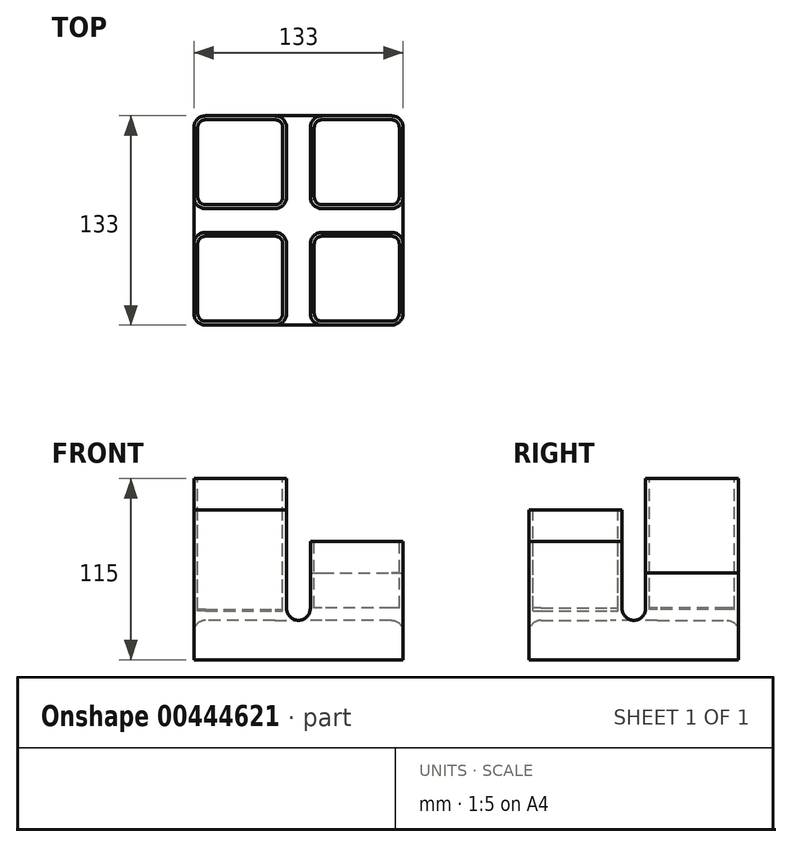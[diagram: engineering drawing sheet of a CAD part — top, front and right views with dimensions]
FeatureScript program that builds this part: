
annotation { "Feature Type Name" : "Feature", "Feature Type Description" : "" }
export const myFeature = defineFeature(function(context is Context, id is Id, definition is map)
    precondition{}
    {
        {
            var Q0;
            Q0=qCreatedBy(makeId("Top.planeOp"),FACE);
            var sketch = newSketch(context, id + "F0", { "sketchPlane" : qUnion([Q0])});
            skLineSegment(sketch, "E0", {"start": v(-102.34, 64.05) * mm, "end": v(-102.34, -68.95) * mm});
            skLineSegment(sketch, "E1", {"start": v(-102.34, -68.95) * mm, "end": v(30.66, -68.95) * mm});
            skLineSegment(sketch, "E2", {"start": v(30.66, -68.95) * mm, "end": v(30.66, 64.05) * mm});
            skLineSegment(sketch, "E3", {"start": v(-102.34, 64.05) * mm, "end": v(30.66, 64.05) * mm});
            skSolve(sketch);
        }
        {
            var Q0;
            Q0 = qSketchRegion(id + "F0", true);
            extrude(context, id + "F1", {"entities" : qUnion([Q0]), "depth" : 25 * mm});
        }
        {
            var Q0;
            Q0=makeQuery(id+"F1.opExtrude","CAP_FACE",FACE,{"disambiguationData":[OSD([sQuery(id+"F0.wireOp",EDGE,"E0"),sQuery(id+"F0.wireOp",EDGE,"E1"),sQuery(id+"F0.wireOp",EDGE,"E2"),sQuery(id+"F0.wireOp",EDGE,"E3")])],"isStart":false});
            var sketch = newSketch(context, id + "F2", { "sketchPlane" : qUnion([Q0])});
            skLineSegment(sketch, "E4", {"start": v(-102.34, 64.05) * mm, "end": v(-102.34, 5.05) * mm});
            skLineSegment(sketch, "E5", {"start": v(-102.34, 5.05) * mm, "end": v(-43.34, 5.05) * mm});
            skLineSegment(sketch, "E6", {"start": v(-43.34, 5.05) * mm, "end": v(-43.34, 64.05) * mm});
            skLineSegment(sketch, "E7", {"start": v(-43.34, 64.05) * mm, "end": v(-102.34, 64.05) * mm});
            skSolve(sketch);
        }
        {
            var Q0;
            Q0=makeQuery(id+"F2.imprint","IMPRINT",FACE,{"disambiguationData":[TD([[makeQuery(id+"F2.imprint","IMPRINT",EDGE,{"derivedFrom":sQuery(id+"F2.wireOp",EDGE,"E4")}),1.0]])]});
            extrude(context, id + "F3", {"entities" : qUnion([Q0]), "operationType" : NewBodyOperationType.ADD, "depth" : 90 * mm});
        }
        {
            var Q0;
            Q0=makeQuery(id+"F1.opExtrude","CAP_FACE",FACE,{"disambiguationData":[OSD([sQuery(id+"F0.wireOp",EDGE,"E0"),sQuery(id+"F0.wireOp",EDGE,"E1"),sQuery(id+"F0.wireOp",EDGE,"E2"),sQuery(id+"F0.wireOp",EDGE,"E3")])],"isStart":false});
            var sketch = newSketch(context, id + "F4", { "sketchPlane" : qUnion([Q0])});
            skLineSegment(sketch, "E8", {"start": v(-102.34, -9.95) * mm, "end": v(-43.34, -9.95) * mm});
            skLineSegment(sketch, "E9", {"start": v(-43.34, -9.95) * mm, "end": v(-43.34, -68.95) * mm});
            skLineSegment(sketch, "E10", {"start": v(-43.34, -68.95) * mm, "end": v(-102.34, -68.95) * mm});
            skLineSegment(sketch, "E11", {"start": v(-102.34, -68.95) * mm, "end": v(-102.34, -9.95) * mm});
            skSolve(sketch);
        }
        {
            var Q0;
            Q0=makeQuery(id+"F4.imprint","IMPRINT",FACE,{"disambiguationData":[TD([[makeQuery(id+"F4.imprint","IMPRINT",EDGE,{"derivedFrom":sQuery(id+"F4.wireOp",EDGE,"E8")}),-1.0]])]});
            extrude(context, id + "F5", {"entities" : qUnion([Q0]), "operationType" : NewBodyOperationType.ADD, "depth" : 70 * mm});
        }
        {
            var Q0;
            Q0=makeQuery(id+"F1.opExtrude","CAP_FACE",FACE,{"disambiguationData":[OSD([sQuery(id+"F0.wireOp",EDGE,"E0"),sQuery(id+"F0.wireOp",EDGE,"E1"),sQuery(id+"F0.wireOp",EDGE,"E2"),sQuery(id+"F0.wireOp",EDGE,"E3")])],"isStart":false});
            var sketch = newSketch(context, id + "F6", { "sketchPlane" : qUnion([Q0])});
            skLineSegment(sketch, "E12", {"start": v(-28.34, -68.95) * mm, "end": v(-28.34, -9.95) * mm});
            skLineSegment(sketch, "E13", {"start": v(-28.34, -9.95) * mm, "end": v(30.66, -9.95) * mm});
            skLineSegment(sketch, "E14", {"start": v(30.66, -9.95) * mm, "end": v(30.66, -68.95) * mm});
            skLineSegment(sketch, "E15", {"start": v(30.66, -68.95) * mm, "end": v(-28.34, -68.95) * mm});
            skSolve(sketch);
        }
        {
            var Q0;
            Q0=makeQuery(id+"F6.imprint","IMPRINT",FACE,{"disambiguationData":[TD([[makeQuery(id+"F6.imprint","IMPRINT",EDGE,{"derivedFrom":sQuery(id+"F6.wireOp",EDGE,"E12")}),-1.0]])]});
            extrude(context, id + "F7", {"entities" : qUnion([Q0]), "operationType" : NewBodyOperationType.ADD, "depth" : 50 * mm});
        }
        {
            var Q0;
            Q0=makeQuery(id+"F1.opExtrude","CAP_FACE",FACE,{"disambiguationData":[OSD([sQuery(id+"F0.wireOp",EDGE,"E0"),sQuery(id+"F0.wireOp",EDGE,"E1"),sQuery(id+"F0.wireOp",EDGE,"E2"),sQuery(id+"F0.wireOp",EDGE,"E3")])],"isStart":false});
            var sketch = newSketch(context, id + "F8", { "sketchPlane" : qUnion([Q0])});
            skLineSegment(sketch, "E16", {"start": v(-28.34, 64.05) * mm, "end": v(-28.34, 5.05) * mm});
            skLineSegment(sketch, "E17", {"start": v(-28.34, 5.05) * mm, "end": v(30.66, 5.05) * mm});
            skLineSegment(sketch, "E18", {"start": v(30.66, 5.05) * mm, "end": v(30.66, 64.05) * mm});
            skLineSegment(sketch, "E19", {"start": v(30.66, 64.05) * mm, "end": v(-28.34, 64.05) * mm});
            skSolve(sketch);
        }
        {
            var Q0;
            Q0=makeQuery(id+"F8.imprint","IMPRINT",FACE,{"disambiguationData":[TD([[makeQuery(id+"F8.imprint","IMPRINT",EDGE,{"derivedFrom":sQuery(id+"F8.wireOp",EDGE,"E16")}),1.0]])]});
            extrude(context, id + "F9", {"entities" : qUnion([Q0]), "operationType" : NewBodyOperationType.ADD, "depth" : 30 * mm});
        }
        {
            var Q0;
            Q0=makeQuery(id+"F9.opExtrude","SWEPT_EDGE",EDGE,{"disambiguationData":[OSD([sQuery(id+"F0.wireOp",EDGE,"E2"),sQuery(id+"F8.wireOp",EDGE,"E17"),sQuery(id+"F8.wireOp",EDGE,"E18")])]});
            var Q1;
            Q1=makeQuery(id+"F9.boolean.opBoolean","MERGE",EDGE,{"derivedFrom":[makeQuery(id+"F1.opExtrude","SWEPT_EDGE",EDGE,{"disambiguationData":[OSD([sQuery(id+"F0.wireOp",EDGE,"E2"),sQuery(id+"F0.wireOp",EDGE,"E3")])]}),makeQuery(id+"F9.opExtrude","SWEPT_EDGE",EDGE,{"disambiguationData":[OSD([sQuery(id+"F8.wireOp",EDGE,"E18"),sQuery(id+"F8.wireOp",EDGE,"E19")])]})]});
            var Q2;
            Q2=makeQuery(id+"F9.opExtrude","SWEPT_EDGE",EDGE,{"disambiguationData":[OSD([sQuery(id+"F0.wireOp",EDGE,"E3"),sQuery(id+"F8.wireOp",EDGE,"E16"),sQuery(id+"F8.wireOp",EDGE,"E19")])]});
            var Q3;
            Q3=makeQuery(id+"F9.opExtrude","SWEPT_EDGE",EDGE,{"disambiguationData":[OSD([sQuery(id+"F8.wireOp",EDGE,"E16"),sQuery(id+"F8.wireOp",EDGE,"E17")])]});
            var Q4;
            Q4=makeQuery(id+"F7.opExtrude","SWEPT_EDGE",EDGE,{"disambiguationData":[OSD([sQuery(id+"F0.wireOp",EDGE,"E2"),sQuery(id+"F6.wireOp",EDGE,"E13"),sQuery(id+"F6.wireOp",EDGE,"E14")])]});
            var Q5;
            Q5=makeQuery(id+"F7.boolean.opBoolean","MERGE",EDGE,{"derivedFrom":[makeQuery(id+"F1.opExtrude","SWEPT_EDGE",EDGE,{"disambiguationData":[OSD([sQuery(id+"F0.wireOp",EDGE,"E1"),sQuery(id+"F0.wireOp",EDGE,"E2")])]}),makeQuery(id+"F7.opExtrude","SWEPT_EDGE",EDGE,{"disambiguationData":[OSD([sQuery(id+"F6.wireOp",EDGE,"E14"),sQuery(id+"F6.wireOp",EDGE,"E15")])]})]});
            var Q6;
            Q6=makeQuery(id+"F7.opExtrude","SWEPT_EDGE",EDGE,{"disambiguationData":[OSD([sQuery(id+"F0.wireOp",EDGE,"E1"),sQuery(id+"F6.wireOp",EDGE,"E12"),sQuery(id+"F6.wireOp",EDGE,"E15")])]});
            var Q7;
            Q7=makeQuery(id+"F7.opExtrude","SWEPT_EDGE",EDGE,{"disambiguationData":[OSD([sQuery(id+"F6.wireOp",EDGE,"E12"),sQuery(id+"F6.wireOp",EDGE,"E13")])]});
            var Q8;
            Q8=makeQuery(id+"F5.opExtrude","SWEPT_EDGE",EDGE,{"disambiguationData":[OSD([sQuery(id+"F4.wireOp",EDGE,"E8"),sQuery(id+"F4.wireOp",EDGE,"E9")])]});
            var Q9;
            Q9=makeQuery(id+"F5.opExtrude","SWEPT_EDGE",EDGE,{"disambiguationData":[OSD([sQuery(id+"F0.wireOp",EDGE,"E1"),sQuery(id+"F4.wireOp",EDGE,"E9"),sQuery(id+"F4.wireOp",EDGE,"E10")])]});
            var Q10;
            Q10=makeQuery(id+"F5.boolean.opBoolean","MERGE",EDGE,{"derivedFrom":[makeQuery(id+"F1.opExtrude","SWEPT_EDGE",EDGE,{"disambiguationData":[OSD([sQuery(id+"F0.wireOp",EDGE,"E0"),sQuery(id+"F0.wireOp",EDGE,"E1")])]}),makeQuery(id+"F5.opExtrude","SWEPT_EDGE",EDGE,{"disambiguationData":[OSD([sQuery(id+"F4.wireOp",EDGE,"E10"),sQuery(id+"F4.wireOp",EDGE,"E11")])]})]});
            var Q11;
            Q11=makeQuery(id+"F5.opExtrude","SWEPT_EDGE",EDGE,{"disambiguationData":[OSD([sQuery(id+"F0.wireOp",EDGE,"E0"),sQuery(id+"F4.wireOp",EDGE,"E8"),sQuery(id+"F4.wireOp",EDGE,"E11")])]});
            var Q12;
            Q12=makeQuery(id+"F3.opExtrude","SWEPT_EDGE",EDGE,{"disambiguationData":[OSD([sQuery(id+"F0.wireOp",EDGE,"E0"),sQuery(id+"F2.wireOp",EDGE,"E4"),sQuery(id+"F2.wireOp",EDGE,"E5")])]});
            var Q13;
            Q13=makeQuery(id+"F3.boolean.opBoolean","MERGE",EDGE,{"derivedFrom":[makeQuery(id+"F1.opExtrude","SWEPT_EDGE",EDGE,{"disambiguationData":[OSD([sQuery(id+"F0.wireOp",EDGE,"E0"),sQuery(id+"F0.wireOp",EDGE,"E3")])]}),makeQuery(id+"F3.opExtrude","SWEPT_EDGE",EDGE,{"disambiguationData":[OSD([sQuery(id+"F2.wireOp",EDGE,"E4"),sQuery(id+"F2.wireOp",EDGE,"E7")])]})]});
            var Q14;
            Q14=makeQuery(id+"F3.opExtrude","SWEPT_EDGE",EDGE,{"disambiguationData":[OSD([sQuery(id+"F0.wireOp",EDGE,"E3"),sQuery(id+"F2.wireOp",EDGE,"E6"),sQuery(id+"F2.wireOp",EDGE,"E7")])]});
            var Q15;
            Q15=makeQuery(id+"F3.opExtrude","SWEPT_EDGE",EDGE,{"disambiguationData":[OSD([sQuery(id+"F2.wireOp",EDGE,"E5"),sQuery(id+"F2.wireOp",EDGE,"E6")])]});
            fillet(context, id + "F10", {"entities" : qUnion([Q0, Q1, Q2, Q3, Q4, Q5, Q6, Q7, Q8, Q9, Q10, Q11, Q12, Q13, Q14, Q15]), "radius" : 7.5 * mm, "tangentPropagation" : true, "allowEdgeOverflow" : false});
        }
        {
            var Q0;
            Q0=makeQuery(id+"F1.opExtrude","CAP_FACE",FACE,{"disambiguationData":[OSD([sQuery(id+"F0.wireOp",EDGE,"E0"),sQuery(id+"F0.wireOp",EDGE,"E1"),sQuery(id+"F0.wireOp",EDGE,"E2"),sQuery(id+"F0.wireOp",EDGE,"E3")])],"isStart":false});
            fillet(context, id + "F11", {"entities" : qUnion([Q0]), "radius" : 7.5 * mm, "tangentPropagation" : true, "allowEdgeOverflow" : false});
        }
        {
            var Q0;
            Q0=makeQuery(id+"F3.opExtrude","CAP_FACE",FACE,{"disambiguationData":[OSD([sQuery(id+"F2.wireOp",EDGE,"E4"),sQuery(id+"F2.wireOp",EDGE,"E5"),sQuery(id+"F2.wireOp",EDGE,"E6"),sQuery(id+"F2.wireOp",EDGE,"E7")])],"isStart":false});
            var sketch = newSketch(context, id + "F12", { "sketchPlane" : qUnion([Q0])});
            skArc(sketch, "E20.0", {"start": v(-99.84, 12.55) * mm, "mid": v(-98.37, 9.01) * mm, "end": v(-94.84, 7.55) * mm});
            skLineSegment(sketch, "E20.1", {"start": v(-99.84, 56.55) * mm, "end": v(-99.84, 12.55) * mm});
            skLineSegment(sketch, "E20.2", {"start": v(-94.84, 7.55) * mm, "end": v(-50.84, 7.55) * mm});
            skArc(sketch, "E20.3", {"start": v(-94.84, 61.55) * mm, "mid": v(-98.37, 60.08) * mm, "end": v(-99.84, 56.55) * mm});
            skArc(sketch, "E20.4", {"start": v(-50.84, 7.55) * mm, "mid": v(-47.3, 9.01) * mm, "end": v(-45.84, 12.55) * mm});
            skLineSegment(sketch, "E20.5", {"start": v(-45.84, 12.55) * mm, "end": v(-45.84, 56.55) * mm});
            skArc(sketch, "E20.6", {"start": v(-45.84, 56.55) * mm, "mid": v(-47.3, 60.08) * mm, "end": v(-50.84, 61.55) * mm});
            skLineSegment(sketch, "E20.7", {"start": v(-50.84, 61.55) * mm, "end": v(-94.84, 61.55) * mm});
            skSolve(sketch);
        }
        {
            var Q0;
            Q0=makeQuery(id+"F12.imprint","IMPRINT",FACE,{"disambiguationData":[TD([[makeQuery(id+"F12.imprint","IMPRINT",EDGE,{"derivedFrom":sQuery(id+"F12.wireOp",EDGE,"E20.0")}),1.0]])]});
            var sketch = newSketch(context, id + "F13", { "sketchPlane" : qUnion([Q0])});
            skSolve(sketch);
        }
        {
            var Q0;
            Q0=makeQuery(id+"F13.imprint","IMPRINT",FACE,{"disambiguationData":[TD([[makeQuery(id+"F13.imprint","IMPRINT",EDGE,{"derivedFrom":makeQuery(id+"F12.imprint","IMPRINT",EDGE,{"derivedFrom":sQuery(id+"F12.wireOp",EDGE,"E20.0")})}),1.0]])]});
            extrude(context, id + "F14", {"entities" : qUnion([Q0]), "operationType" : NewBodyOperationType.REMOVE, "oppositeDirection" : true, "depth" : 83 * mm});
        }
        {
            var Q0;
            Q0=makeQuery(id+"F5.opExtrude","CAP_FACE",FACE,{"disambiguationData":[OSD([sQuery(id+"F4.wireOp",EDGE,"E8"),sQuery(id+"F4.wireOp",EDGE,"E9"),sQuery(id+"F4.wireOp",EDGE,"E10"),sQuery(id+"F4.wireOp",EDGE,"E11")])],"isStart":false});
            var sketch = newSketch(context, id + "F15", { "sketchPlane" : qUnion([Q0])});
            skArc(sketch, "E21.0", {"start": v(-50.84, -66.45) * mm, "mid": v(-47.3, -64.99) * mm, "end": v(-45.84, -61.45) * mm});
            skLineSegment(sketch, "E21.1", {"start": v(-94.84, -66.45) * mm, "end": v(-50.84, -66.45) * mm});
            skLineSegment(sketch, "E21.2", {"start": v(-45.84, -61.45) * mm, "end": v(-45.84, -17.45) * mm});
            skArc(sketch, "E21.3", {"start": v(-99.84, -61.45) * mm, "mid": v(-98.37, -64.99) * mm, "end": v(-94.84, -66.45) * mm});
            skArc(sketch, "E21.4", {"start": v(-45.84, -17.45) * mm, "mid": v(-47.3, -13.92) * mm, "end": v(-50.84, -12.45) * mm});
            skLineSegment(sketch, "E21.5", {"start": v(-50.84, -12.45) * mm, "end": v(-94.84, -12.45) * mm});
            skArc(sketch, "E21.6", {"start": v(-94.84, -12.45) * mm, "mid": v(-98.37, -13.92) * mm, "end": v(-99.84, -17.45) * mm});
            skLineSegment(sketch, "E21.7", {"start": v(-99.84, -17.45) * mm, "end": v(-99.84, -61.45) * mm});
            skSolve(sketch);
        }
        {
            var Q0;
            Q0=makeQuery(id+"F15.imprint","IMPRINT",FACE,{"disambiguationData":[TD([[makeQuery(id+"F15.imprint","IMPRINT",EDGE,{"derivedFrom":sQuery(id+"F15.wireOp",EDGE,"E21.0")}),1.0]])]});
            extrude(context, id + "F16", {"entities" : qUnion([Q0]), "operationType" : NewBodyOperationType.REMOVE, "oppositeDirection" : true, "depth" : 64 * mm});
        }
        {
            var Q0;
            Q0=makeQuery(id+"F7.opExtrude","CAP_FACE",FACE,{"disambiguationData":[OSD([sQuery(id+"F6.wireOp",EDGE,"E12"),sQuery(id+"F6.wireOp",EDGE,"E13"),sQuery(id+"F6.wireOp",EDGE,"E14"),sQuery(id+"F6.wireOp",EDGE,"E15")])],"isStart":false});
            var sketch = newSketch(context, id + "F17", { "sketchPlane" : qUnion([Q0])});
            skArc(sketch, "E22.0", {"start": v(28.16, -17.45) * mm, "mid": v(26.7, -13.92) * mm, "end": v(23.16, -12.45) * mm});
            skLineSegment(sketch, "E22.1", {"start": v(28.16, -61.45) * mm, "end": v(28.16, -17.45) * mm});
            skLineSegment(sketch, "E22.2", {"start": v(23.16, -12.45) * mm, "end": v(-20.84, -12.45) * mm});
            skArc(sketch, "E22.3", {"start": v(23.16, -66.45) * mm, "mid": v(26.7, -64.99) * mm, "end": v(28.16, -61.45) * mm});
            skArc(sketch, "E22.4", {"start": v(-20.84, -12.45) * mm, "mid": v(-24.37, -13.92) * mm, "end": v(-25.84, -17.45) * mm});
            skLineSegment(sketch, "E22.5", {"start": v(-25.84, -17.45) * mm, "end": v(-25.84, -61.45) * mm});
            skArc(sketch, "E22.6", {"start": v(-25.84, -61.45) * mm, "mid": v(-24.37, -64.99) * mm, "end": v(-20.84, -66.45) * mm});
            skLineSegment(sketch, "E22.7", {"start": v(-20.84, -66.45) * mm, "end": v(23.16, -66.45) * mm});
            skSolve(sketch);
        }
        {
            var Q0;
            Q0=makeQuery(id+"F17.imprint","IMPRINT",FACE,{"disambiguationData":[TD([[makeQuery(id+"F17.imprint","IMPRINT",EDGE,{"derivedFrom":sQuery(id+"F17.wireOp",EDGE,"E22.0")}),1.0]])]});
            extrude(context, id + "F18", {"entities" : qUnion([Q0]), "operationType" : NewBodyOperationType.REMOVE, "oppositeDirection" : true, "depth" : 42 * mm});
        }
        {
            var Q0;
            Q0=makeQuery(id+"F9.opExtrude","CAP_FACE",FACE,{"disambiguationData":[OSD([sQuery(id+"F8.wireOp",EDGE,"E16"),sQuery(id+"F8.wireOp",EDGE,"E17"),sQuery(id+"F8.wireOp",EDGE,"E18"),sQuery(id+"F8.wireOp",EDGE,"E19")])],"isStart":false});
            var sketch = newSketch(context, id + "F19", { "sketchPlane" : qUnion([Q0])});
            skArc(sketch, "E23.0", {"start": v(-20.84, 61.55) * mm, "mid": v(-24.37, 60.08) * mm, "end": v(-25.84, 56.55) * mm});
            skLineSegment(sketch, "E23.1", {"start": v(23.16, 61.55) * mm, "end": v(-20.84, 61.55) * mm});
            skLineSegment(sketch, "E23.2", {"start": v(-25.84, 56.55) * mm, "end": v(-25.84, 12.55) * mm});
            skArc(sketch, "E23.3", {"start": v(28.16, 56.55) * mm, "mid": v(26.7, 60.08) * mm, "end": v(23.16, 61.55) * mm});
            skArc(sketch, "E23.4", {"start": v(-25.84, 12.55) * mm, "mid": v(-24.37, 9.01) * mm, "end": v(-20.84, 7.55) * mm});
            skLineSegment(sketch, "E23.5", {"start": v(-20.84, 7.55) * mm, "end": v(23.16, 7.55) * mm});
            skArc(sketch, "E23.6", {"start": v(23.16, 7.55) * mm, "mid": v(26.7, 9.01) * mm, "end": v(28.16, 12.55) * mm});
            skLineSegment(sketch, "E23.7", {"start": v(28.16, 12.55) * mm, "end": v(28.16, 56.55) * mm});
            skSolve(sketch);
        }
        {
            var Q0;
            Q0=makeQuery(id+"F19.imprint","IMPRINT",FACE,{"disambiguationData":[TD([[makeQuery(id+"F19.imprint","IMPRINT",EDGE,{"derivedFrom":sQuery(id+"F19.wireOp",EDGE,"E23.0")}),1.0]])]});
            extrude(context, id + "F20", {"entities" : qUnion([Q0]), "operationType" : NewBodyOperationType.REMOVE, "oppositeDirection" : true, "depth" : 22 * mm});
        }
    });
